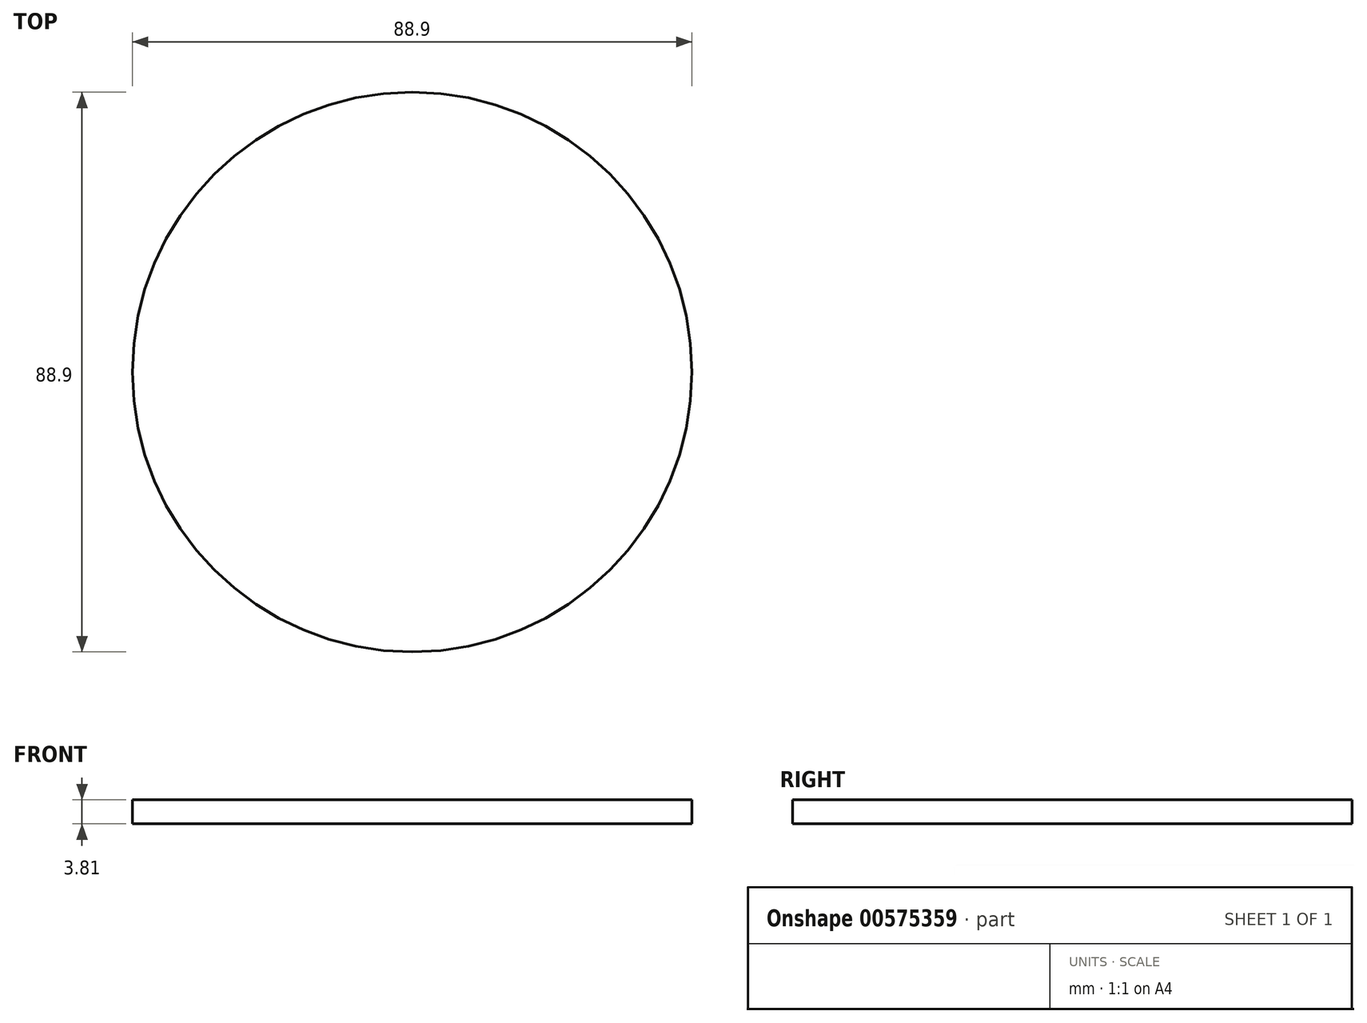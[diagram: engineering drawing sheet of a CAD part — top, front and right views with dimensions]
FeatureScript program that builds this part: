
annotation { "Feature Type Name" : "Feature", "Feature Type Description" : "" }
export const myFeature = defineFeature(function(context is Context, id is Id, definition is map)
    precondition{}
    {
        {
            var Q0;
            Q0=qCreatedBy(makeId("Top.planeOp"),FACE);
            var sketch = newSketch(context, id + "F0", { "sketchPlane" : qUnion([Q0])});
            skCircle(sketch, "E0", {"center": v(0, 0) * mm, "radius": 44.45 * mm});
            skSolve(sketch);
        }
        {
            var Q0;
            Q0=makeQuery(id+"F0.imprint","IMPRINT",FACE,{"disambiguationData":[TD([[makeQuery(id+"F0.imprint","IMPRINT",EDGE,{"derivedFrom":sQuery(id+"F0.wireOp",EDGE,"E0")}),1.0]])]});
            extrude(context, id + "F1", {"entities" : qUnion([Q0]), "depth" : 3.8 * mm, "offsetDistance" : 25.4 * mm});
        }
    });
